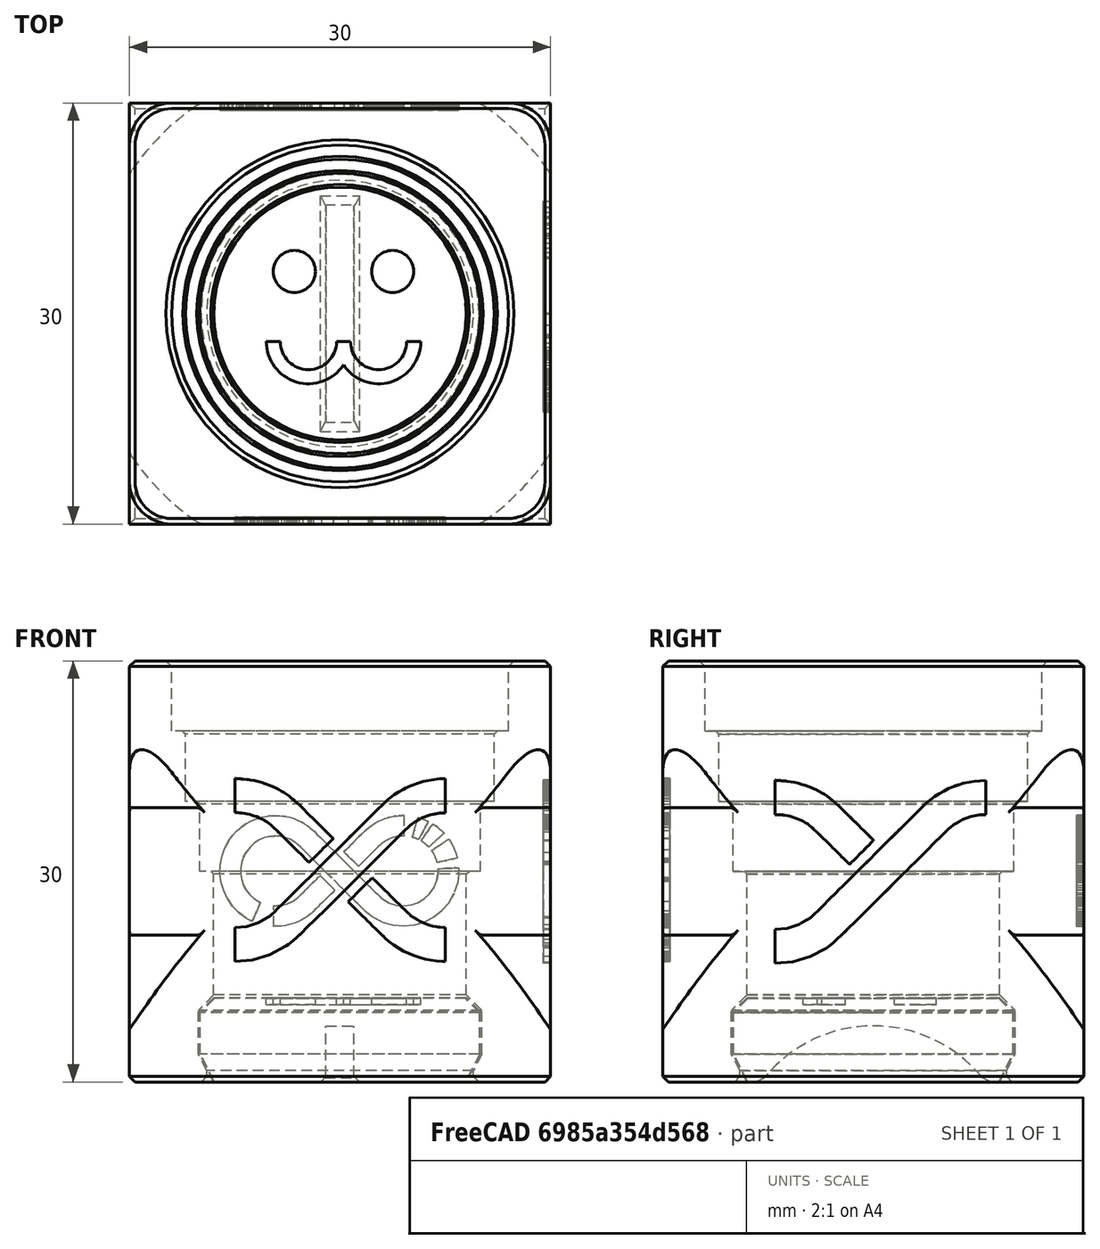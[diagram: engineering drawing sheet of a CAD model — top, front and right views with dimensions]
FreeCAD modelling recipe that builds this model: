
FCSTD DOCUMENT  (FreeCAD 0.19R24291 (Git))
Label: test-cube
License: Other
LicenseURL: GPL3
objects: Part::Cylinder×24, Part::Chamfer×20, Part::Cut×18, Part::MultiFuse×10, Part::Feature×8, TechDraw::DrawViewDimension×8, Part::Box×6, Part::MultiCommon×6, Part::Fillet×4, Part::FeaturePython×4, TechDraw::DrawViewPart×4, Part::Cone×2, TechDraw::DrawSVGTemplate×1, TechDraw::DrawViewSection×1, TechDraw::DrawViewBalloon×1, TechDraw::DrawPage×1
note: 102 computed .brp shape members not serialized (recipe doc carries the construction recipe); baked Part::Feature solids carry a one-line shape summary decoded from their .brp

FEATURE [Part::Box] Box  label="Cube"
  AttacherType = Attacher::AttachEngine3D
  Height = 12
  Length = 30
  Width = 30
FEATURE [Part::Cylinder] Cylinder
  Angle = 360
  AttacherType = Attacher::AttachEngine3D
  Height = 30
  Placement = pos=(15,15,0) rot=(0,0,1;0rad)
  Radius = 18
FEATURE [Part::Box] Box002  label="Cube002"
  AttacherType = Attacher::AttachEngine3D
  Height = 30
  Length = 30
  Width = 30
FEATURE [Part::Cone] Cone
  Angle = 360
  AttacherType = Attacher::AttachEngine3D
  Height = 23
  Placement = pos=(15,15,0) rot=(0,0,1;0rad)
  Radius1 = 23
  Radius2 = 12
FEATURE [Part::MultiCommon] Common001
  Shapes = -> [Cone,Box]
FEATURE [Part::Feature] Common001001
  Placement = pos=(30,0,30) rot=(0,1,0;3.14159rad)
  shape: bbox 36.87 x 36.87 x 12 mm, 10 faces (baked)
FEATURE [Part::MultiCommon] Common
  Shapes = -> [Box002,Cylinder]
FEATURE [Part::Fillet] Fillet
  Base = -> Common001001
  Edges = 4 edges r=3: [Edge11,Edge13,Edge15,Edge18]
FEATURE [Part::Cylinder] Cylinder001
  Angle = 360
  AttacherType = Attacher::AttachEngine3D
  Height = 12
  Placement = pos=(15,15,9) rot=(0,0,1;0rad)
  Radius = 20
FEATURE [Part::MultiCommon] Common001002
  Shapes = -> [Cylinder001,Common]
FEATURE [Part::Fillet] Fillet001
  Base = -> Common001002
  Edges = 8 edges r=1: [Edge9,Edge11,Edge13,Edge15,Edge17,Edge19,Edge21,Edge23]
FEATURE [Part::Chamfer] Chamfer
  Base = -> Common001
  Edges = 4 edges r=0.4: [Edge14,Edge17,Edge21,Edge24]
FEATURE [Part::Chamfer] Chamfer001
  Base = -> Fillet
  Edges = 8 edges r=0.4: [Edge6,Edge10,Edge20,Edge21,Edge22,Edge23,Edge24,Edge25]
FEATURE [Part::MultiFuse] Fusion
  Shapes = -> [Chamfer001,Chamfer,Fillet001]
FEATURE [Part::Cylinder] Cylinder004
  Angle = 360
  AttacherType = Attacher::AttachEngine3D
  Height = 7
  Placement = pos=(15,15,0) rot=(0,0,1;0rad)
  Radius = 10.1
FEATURE [Part::Cylinder] Cylinder005
  Angle = 360
  AttacherType = Attacher::AttachEngine3D
  Height = 6
  Placement = pos=(15,15,0) rot=(0,0,1;0rad)
  Radius = 10
FEATURE [Part::Chamfer] Chamfer002003
  Base = -> Cylinder005
  Edges = 1 edges: [Edge3 r1=2 r2=1]
FEATURE [Part::Chamfer] Chamfer002004
  Base = -> Chamfer002003
  Edges = 1 edges r=1: [Edge2]
FEATURE [Part::Chamfer] Chamfer002005
  Base = -> Cylinder004
  Edges = 1 edges: [Edge3 r1=2 r2=1]
FEATURE [Part::Cut] Cut
  Base = -> Fusion
  Tool = -> Chamfer002005
FEATURE [Part::Cylinder] Cylinder006
  Angle = 360
  AttacherType = Attacher::AttachEngine3D
  Height = 6
  Placement = pos=(15,15,0) rot=(0,0,1;0rad)
  Radius = 9.5
FEATURE [Part::Cut] Cut001
  Base = -> Cut
  Tool = -> Cylinder006
FEATURE [Part::Chamfer] Chamfer002006
  Base = -> Cut001
  Edges = 1 edges r=0.4: [Edge157]
FEATURE [Part::Chamfer] Chamfer002007
  Base = -> Chamfer002006
  Edges = 1 edges r=1.9: [Edge69]
FEATURE [Part::Cylinder] Cylinder007
  Angle = 360
  AttacherType = Attacher::AttachEngine3D
  Height = 2
  Placement = pos=(14,15,-6) rot=(0,1,0;1.5708rad)
  Radius = 10
FEATURE [Part::Cut] Cut002
  Base = -> Chamfer002004
  Tool = -> Cylinder007
FEATURE [Part::Chamfer] Chamfer002008
  Base = -> Cut002
  Edges = 4 edges r=0.4: [Edge8,Edge9,Edge10,Edge11]
FEATURE [Part::Cylinder] Cylinder008
  Angle = 360
  AttacherType = Attacher::AttachEngine3D
  Height = 33
  Placement = pos=(15,15,0) rot=(0,0,1;0rad)
  Radius = 9
FEATURE [Part::Cylinder] Cylinder009
  Angle = 360
  AttacherType = Attacher::AttachEngine3D
  Height = 33
  Placement = pos=(15,15,15) rot=(0,0,1;0rad)
  Radius = 10
FEATURE [Part::Cylinder] Cylinder010
  Angle = 360
  AttacherType = Attacher::AttachEngine3D
  Height = 33
  Placement = pos=(15,15,20) rot=(0,0,1;0rad)
  Radius = 11
FEATURE [Part::Cylinder] Cylinder011
  Angle = 360
  AttacherType = Attacher::AttachEngine3D
  Height = 33
  Placement = pos=(15,15,25) rot=(0,0,1;0rad)
  Radius = 12
FEATURE [Part::MultiFuse] Fusion001
  Shapes = -> [Cylinder011,Cylinder010,Cylinder009,Cylinder008]
FEATURE [Part::Cut] Cut003
  Base = -> Chamfer002007
  Refine = true
  Tool = -> Fusion001
FEATURE [Part::Chamfer] Chamfer002009
  Base = -> Cut003
  Edges = 3 edges r=0.2: [Edge81,Edge87,Edge102]
FEATURE [Part::Chamfer] Chamfer002010
  Base = -> Chamfer002009
  Edges = 1 edges r=0.4: [Edge79]
FEATURE [Part::Feature] Funky_Juttuli_Bombul_1_001001_solid  label="x"
  Placement = pos=(5.5,0.5,14.5) rot=(1,0,0;1.5708rad)
  shape: bbox 20 x 2 x 20 mm, 335 faces (baked)
FEATURE [Part::Feature] Funky_Juttuli_Bombul_2_001001_solid  label="y"
  Placement = pos=(29.5,-20,13.5) rot=(0.57735,0.57735,0.57735;2.0944rad)
  shape: bbox 2 x 20 x 20 mm, 246 faces (baked)
FEATURE [Part::Feature] Funky_Juttuli_Bombul001001_solid  label="logo"
  Placement = pos=(24.6,29.5,21) rot=(0,0.707107,0.707107;3.14159rad)
  shape: bbox 20 x 2 x 20 mm, 931 faces (baked)
FEATURE [Part::Cut] Cut004
  Base = -> Chamfer002010
  Tool = -> Funky_Juttuli_Bombul001001_solid
FEATURE [Part::Cut] Cut005
  Base = -> Cut004
  Tool = -> Funky_Juttuli_Bombul_2_001001_solid
FEATURE [Part::Cut] Cut006
  Base = -> Cut005
  Tool = -> Funky_Juttuli_Bombul_1_001001_solid
FEATURE [Part::FeaturePython] Tube  # WARN: FeaturePython — macro-defined, semantics opaque (R4)
  AttacherType = Attacher::AttachEngine3D
  Height = 1
  InnerRadius = 2
  OuterRadius = 3
  Placement = pos=(13,11.5,5.5) rot=(0,0,1;0rad)
FEATURE [Part::FeaturePython] Tube001  # WARN: FeaturePython — macro-defined, semantics opaque (R4)
  AttacherType = Attacher::AttachEngine3D
  Height = 1
  InnerRadius = 2
  OuterRadius = 3
  Placement = pos=(18,11.5,5.5) rot=(0,0,1;0rad)
FEATURE [Part::Cylinder] Cylinder012
  Angle = 360
  AttacherType = Attacher::AttachEngine3D
  Height = 1
  Placement = pos=(11.75,18,5.5) rot=(0,0,1;0rad)
  Radius = 1.5
FEATURE [Part::Cylinder] Cylinder013
  Angle = 360
  AttacherType = Attacher::AttachEngine3D
  Height = 1
  Placement = pos=(18.75,18,5.5) rot=(0,0,1;0rad)
  Radius = 1.5
FEATURE [Part::MultiFuse] Fusion002
  Shapes = -> [Tube001,Tube]
FEATURE [Part::Box] Box003  label="Cube003"
  AttacherType = Attacher::AttachEngine3D
  Height = 10
  Length = 16
  Placement = pos=(9.5,11.5,0) rot=(0,0,1;0rad)
  Width = 10
FEATURE [Part::Cut] Cut007
  Base = -> Fusion002
  Placement = pos=(-0.25,1.5,0) rot=(0,0,1;0rad)
  Tool = -> Box003
FEATURE [Part::MultiFuse] Fusion003
  Shapes = -> [Cut007,Cylinder013,Cylinder012]
FEATURE [Part::Cut] Cut008
  Base = -> Chamfer002008
  Refine = true
  Tool = -> Fusion003
FEATURE [TechDraw::DrawSVGTemplate] Template
  EditableTexts = Designed_by_Name=Chip; Drawing_number=-; FC-Date=2022-03-12; FC-SC=1:1.5; FC-SH=1/1; FC-Title=SnakeOil test cube; Subtitle=-; Weight=-
  Height = 210
  Orientation = 1
  Width = 297
FEATURE [Part::MultiFuse] Fusion004
  Shapes = -> [Cut008,Cut006]
FEATURE [TechDraw::DrawViewPart] View
  CoarseView = false
  Direction = (0.577,-0.577,0.577)
  Focus = 100
  HardHidden = false
  IsoCount = 0
  IsoHidden = false
  IsoVisible = false
  LockPosition = false
  Perspective = false
  Rotation = 0
  Scale = 1.5
  ScaleType = 0
  SeamHidden = false
  SeamVisible = true
  SmoothHidden = false
  SmoothVisible = true
  Source = -> [Fusion004]
  X = 53.1184
  XDirection = (0.707,0.707,0)
  Y = 155.57
FEATURE [TechDraw::DrawViewPart] View001
  CoarseView = false
  Direction = (0,0,1)
  Focus = 100
  HardHidden = false
  IsoCount = 0
  IsoHidden = false
  IsoVisible = false
  LockPosition = false
  Perspective = false
  Rotation = 0
  Scale = 1.5
  ScaleType = 0
  SeamHidden = false
  SeamVisible = true
  SmoothHidden = false
  SmoothVisible = true
  Source = -> [Fusion004]
  X = 142.764
  XDirection = (1,0,0)
  Y = 157.287
FEATURE [TechDraw::DrawViewPart] View002
  CoarseView = false
  Direction = (1,0,0)
  Focus = 100
  HardHidden = false
  IsoCount = 0
  IsoHidden = false
  IsoVisible = false
  LockPosition = false
  Perspective = false
  Rotation = 0
  Scale = 1.5
  ScaleType = 0
  SeamHidden = false
  SeamVisible = true
  SmoothHidden = false
  SmoothVisible = true
  Source = -> [Fusion004]
  X = 216.819
  XDirection = (0,1,0)
  Y = 157.983
FEATURE [TechDraw::DrawViewSection] SectionView  label="Section  - "
  BaseView = -> View002
  CoarseView = false
  CutSurfaceDisplay = 2
  Direction = (0,0,-1)
  FileGeomPattern = <path>
  FileHatchPattern = <path>
  Focus = 100
  FuseBeforeCut = false
  HardHidden = false
  HatchScale = 1
  IsoCount = 0
  IsoHidden = false
  IsoVisible = false
  LockPosition = false
  NameGeomPattern = Diamond
  Perspective = false
  Rotation = 0
  Scale = 1.5
  ScaleType = 0
  SeamHidden = false
  SeamVisible = true
  SectionDirection = 2
  SectionNormal = (0,0,-1)
  SectionOrigin = (15,15,15)
  SmoothHidden = false
  SmoothVisible = true
  Source = -> [Fusion004]
  X = 219.64
  XDirection = (0,1,0)
  Y = 91.1156
FEATURE [TechDraw::DrawViewDimension] Dimension
  Arbitrary = false
  ArbitraryTolerances = false
  EqualTolerance = true
  FormatSpec = %.2f
  FormatSpecOverTolerance = %+.2f
  FormatSpecUnderTolerance = %+.2f
  Inverted = false
  LockPosition = false
  MeasureType = 1
  OverTolerance = 0
  References2D = -> [View001]
  Rotation = 0
  ScaleType = 0
  TheoreticalExact = false
  Type = 1
  UnderTolerance = 0
  X = -0.329799
  Y = 34.2334
FEATURE [TechDraw::DrawViewDimension] Dimension001
  Arbitrary = false
  ArbitraryTolerances = false
  EqualTolerance = true
  FormatSpec = %.2f
  FormatSpecOverTolerance = %+.2f
  FormatSpecUnderTolerance = %+.2f
  Inverted = false
  LockPosition = false
  MeasureType = 1
  OverTolerance = 0
  References2D = -> [View001]
  Rotation = 0
  ScaleType = 0
  TheoreticalExact = false
  Type = 2
  UnderTolerance = 0
  X = 28.2238
  Y = 1.24591
FEATURE [TechDraw::DrawViewDimension] Dimension002
  Arbitrary = false
  ArbitraryTolerances = false
  EqualTolerance = true
  FormatSpec = ⌀%.2f
  FormatSpecOverTolerance = %+.2f
  FormatSpecUnderTolerance = %+.2f
  Inverted = false
  LockPosition = false
  MeasureType = 1
  OverTolerance = 0
  References2D = -> [View001]
  Rotation = 0
  ScaleType = 0
  TheoreticalExact = false
  Type = 5
  UnderTolerance = 0
  X = -30.9115
  Y = -26.0853
FEATURE [TechDraw::DrawViewDimension] Dimension003
  Arbitrary = false
  ArbitraryTolerances = false
  EqualTolerance = true
  FormatSpec = ⌀%.2f
  FormatSpecOverTolerance = %+.2f
  FormatSpecUnderTolerance = %+.2f
  Inverted = false
  LockPosition = false
  MeasureType = 1
  OverTolerance = 0
  References2D = -> [View001]
  Rotation = 0
  ScaleType = 0
  TheoreticalExact = false
  Type = 5
  UnderTolerance = 0
  X = -34.7096
  Y = -19.8838
FEATURE [TechDraw::DrawViewDimension] Dimension004
  Arbitrary = false
  ArbitraryTolerances = false
  EqualTolerance = true
  FormatSpec = ⌀%.2f
  FormatSpecOverTolerance = %+.2f
  FormatSpecUnderTolerance = %+.2f
  Inverted = false
  LockPosition = false
  MeasureType = 1
  OverTolerance = 0
  References2D = -> [View001]
  Rotation = 0
  ScaleType = 0
  TheoreticalExact = false
  Type = 5
  UnderTolerance = 0
  X = -38.0246
  Y = -13.1141
FEATURE [TechDraw::DrawViewDimension] Dimension005
  Arbitrary = false
  ArbitraryTolerances = false
  EqualTolerance = true
  FormatSpec = ⌀%.2f
  FormatSpecOverTolerance = %+.2f
  FormatSpecUnderTolerance = %+.2f
  Inverted = false
  LockPosition = false
  MeasureType = 1
  OverTolerance = 0
  References2D = -> [View001]
  Rotation = 0
  ScaleType = 0
  TheoreticalExact = false
  Type = 5
  UnderTolerance = 0
  X = -40.1538
  Y = -5.34316
FEATURE [TechDraw::DrawViewDimension] Dimension006
  Arbitrary = false
  ArbitraryTolerances = false
  EqualTolerance = true
  FormatSpec = %.2f
  FormatSpecOverTolerance = %+.2f
  FormatSpecUnderTolerance = %+.2f
  Inverted = false
  LockPosition = false
  MeasureType = 1
  OverTolerance = 0
  References2D = -> [View002]
  Rotation = 0
  ScaleType = 0
  TheoreticalExact = false
  Type = 2
  UnderTolerance = 0
  X = 36.8069
  Y = 0.263839
FEATURE [TechDraw::DrawViewDimension] Dimension007
  Arbitrary = false
  ArbitraryTolerances = false
  EqualTolerance = true
  FormatSpec = ⌀%.2f
  FormatSpecOverTolerance = %+.2f
  FormatSpecUnderTolerance = %+.2f
  Inverted = false
  LockPosition = false
  MeasureType = 1
  OverTolerance = 0
  References2D = -> [SectionView]
  Rotation = 0
  ScaleType = 0
  TheoreticalExact = false
  Type = 5
  UnderTolerance = 0
  X = 28.9918
  Y = -24.4224
FEATURE [TechDraw::DrawViewPart] View003
  CoarseView = false
  Direction = (0,0,-1)
  Focus = 100
  HardHidden = false
  IsoCount = 0
  IsoHidden = false
  IsoVisible = false
  LockPosition = false
  Perspective = false
  Rotation = 0
  Scale = 1.5
  ScaleType = 0
  SeamHidden = false
  SeamVisible = true
  SmoothHidden = false
  SmoothVisible = true
  Source = -> [Fusion004]
  X = 144.045
  XDirection = (1,0,0)
  Y = 90.5135
FEATURE [TechDraw::DrawViewBalloon] Balloon
  BubbleShape = 1
  EndType = 0
  EndTypeScale = 1
  KinkLength = 5
  LockPosition = false
  OriginX = -6.8407
  OriginY = 6.58082
  Rotation = 0
  ScaleType = 0
  ShapeScale = 1
  SourceView = -> View003
  Text = 0.15mm gap
  TextWrapLen = -1
  X = -25.924
  Y = 10.758
FEATURE [TechDraw::DrawPage] Page
  KeepUpdated = true
  NextBalloonIndex = 2
  ProjectionType = 0
  Template = -> Template
  Views = -> [View,View001,View002,SectionView,Dimension,Dimension001,Dimension002,Dimension003,Dimension004,Dimension005,Dimension006,Dimension007,View003,Balloon]
FEATURE [Part::Cylinder] Cylinder014
  Angle = 360
  AttacherType = Attacher::AttachEngine3D
  Height = 1
  Placement = pos=(18.75,18,5.5) rot=(0,0,1;0rad)
  Radius = 1.5
FEATURE [Part::Box] Box004  label="Cube004"
  AttacherType = Attacher::AttachEngine3D
  Height = 12
  Length = 30
  Width = 30
FEATURE [Part::Box] Box005  label="Cube005"
  AttacherType = Attacher::AttachEngine3D
  Height = 30
  Length = 30
  Width = 30
FEATURE [Part::Cylinder] Cylinder015
  Angle = 360
  AttacherType = Attacher::AttachEngine3D
  Height = 30
  Placement = pos=(15,15,0) rot=(0,0,1;0rad)
  Radius = 18
FEATURE [Part::Cone] Cone001
  Angle = 360
  AttacherType = Attacher::AttachEngine3D
  Height = 23
  Placement = pos=(15,15,0) rot=(0,0,1;0rad)
  Radius1 = 23
  Radius2 = 12
FEATURE [Part::Cylinder] Cylinder016
  Angle = 360
  AttacherType = Attacher::AttachEngine3D
  Height = 12
  Placement = pos=(15,15,9) rot=(0,0,1;0rad)
  Radius = 20
FEATURE [Part::MultiCommon] Common001003
  Shapes = -> [Cone001,Box004]
FEATURE [Part::Feature] Common001004
  Placement = pos=(30,0,30) rot=(0,1,0;3.14159rad)
  shape: bbox 36.87 x 36.87 x 12 mm, 10 faces (baked)
FEATURE [Part::MultiCommon] Common001005
  Shapes = -> [Box005,Cylinder015]
FEATURE [Part::Fillet] Fillet002
  Base = -> Common001004
  Edges = 4 edges r=3: [Edge11,Edge13,Edge15,Edge18]
FEATURE [Part::MultiCommon] Common001006
  Shapes = -> [Cylinder016,Common001005]
FEATURE [Part::Fillet] Fillet003
  Base = -> Common001006
  Edges = 8 edges r=1: [Edge9,Edge11,Edge13,Edge15,Edge17,Edge19,Edge21,Edge23]
FEATURE [Part::Cylinder] Cylinder017
  Angle = 360
  AttacherType = Attacher::AttachEngine3D
  Height = 33
  Placement = pos=(15,15,15) rot=(0,0,1;0rad)
  Radius = 10
FEATURE [Part::Cylinder] Cylinder018
  Angle = 360
  AttacherType = Attacher::AttachEngine3D
  Height = 6
  Placement = pos=(15,15,0) rot=(0,0,1;0rad)
  Radius = 9.5
FEATURE [Part::Cylinder] Cylinder019
  Angle = 360
  AttacherType = Attacher::AttachEngine3D
  Height = 33
  Placement = pos=(15,15,0) rot=(0,0,1;0rad)
  Radius = 9
FEATURE [Part::Feature] Funky_Juttuli_Bombul_1_001001_solid001  label="x001"
  Placement = pos=(5.5,0.5,14.5) rot=(1,0,0;1.5708rad)
  shape: bbox 20 x 2 x 20 mm, 335 faces (baked)
FEATURE [Part::Cylinder] Cylinder020
  Angle = 360
  AttacherType = Attacher::AttachEngine3D
  Height = 33
  Placement = pos=(15,15,20) rot=(0,0,1;0rad)
  Radius = 11
FEATURE [Part::FeaturePython] Tube002  # WARN: FeaturePython — macro-defined, semantics opaque (R4)
  AttacherType = Attacher::AttachEngine3D
  Height = 1
  InnerRadius = 2
  OuterRadius = 3
  Placement = pos=(18,11.5,5.5) rot=(0,0,1;0rad)
FEATURE [Part::Feature] Funky_Juttuli_Bombul001001_solid001  label="logo001"
  Placement = pos=(24.6,29.5,21) rot=(0,0.707107,0.707107;3.14159rad)
  shape: bbox 20 x 2 x 20 mm, 931 faces (baked)
FEATURE [Part::Cylinder] Cylinder021
  Angle = 360
  AttacherType = Attacher::AttachEngine3D
  Height = 5.95
  Placement = pos=(15,15,0) rot=(0,0,1;0rad)
  Radius = 9.95
FEATURE [Part::Cylinder] Cylinder022
  Angle = 360
  AttacherType = Attacher::AttachEngine3D
  Height = 7
  Placement = pos=(15,15,0) rot=(0,0,1;0rad)
  Radius = 10.1
FEATURE [Part::Chamfer] Chamfer002014
  Base = -> Cylinder022
  Edges = 1 edges: [Edge3 r1=2 r2=1]
FEATURE [Part::Cylinder] Cylinder023
  Angle = 360
  AttacherType = Attacher::AttachEngine3D
  Height = 33
  Placement = pos=(15,15,25) rot=(0,0,1;0rad)
  Radius = 12
FEATURE [Part::Cylinder] Cylinder024
  Angle = 360
  AttacherType = Attacher::AttachEngine3D
  Height = 2
  Placement = pos=(14,15,-6) rot=(0,1,0;1.5708rad)
  Radius = 10
FEATURE [Part::Chamfer] Chamfer002019
  Base = -> Fillet002
  Edges = 8 edges r=0.4: [Edge6,Edge10,Edge20,Edge21,Edge22,Edge23,Edge24,Edge25]
FEATURE [Part::MultiFuse] Fusion007
  Shapes = -> [Cylinder023,Cylinder020,Cylinder017,Cylinder019]
FEATURE [Part::Chamfer] Chamfer002020
  Base = -> Common001003
  Edges = 4 edges r=0.4: [Edge14,Edge17,Edge21,Edge24]
FEATURE [Part::MultiFuse] Fusion005
  Shapes = -> [Chamfer002019,Chamfer002020,Fillet003]
FEATURE [Part::Cut] Cut014
  Base = -> Fusion005
  Tool = -> Chamfer002014
FEATURE [Part::Cut] Cut009
  Base = -> Cut014
  Tool = -> Cylinder018
FEATURE [Part::Chamfer] Chamfer002015
  Base = -> Cut009
  Edges = 1 edges r=0.4: [Edge157]
FEATURE [Part::Chamfer] Chamfer002017
  Base = -> Chamfer002015
  Edges = 1 edges r=1.9: [Edge69]
FEATURE [Part::Cut] Cut010
  Base = -> Chamfer002017
  Refine = true
  Tool = -> Fusion007
FEATURE [Part::Chamfer] Chamfer002016
  Base = -> Cut010
  Edges = 3 edges r=0.2: [Edge81,Edge87,Edge102]
FEATURE [Part::Chamfer] Chamfer002011
  Base = -> Chamfer002016
  Edges = 1 edges r=0.4: [Edge79]
FEATURE [Part::Cut] Cut013
  Base = -> Chamfer002011
  Tool = -> Funky_Juttuli_Bombul001001_solid001
FEATURE [Part::Feature] Funky_Juttuli_Bombul_2_001001_solid001  label="y001"
  Placement = pos=(29.5,-20,13.5) rot=(0.57735,0.57735,0.57735;2.0944rad)
  shape: bbox 2 x 20 x 20 mm, 246 faces (baked)
FEATURE [Part::Cut] Cut011
  Base = -> Cut013
  Tool = -> Funky_Juttuli_Bombul_2_001001_solid001
FEATURE [Part::Cut] Cut015
  Base = -> Cut011
  Tool = -> Funky_Juttuli_Bombul_1_001001_solid001
FEATURE [Part::Box] Box006  label="Cube006"
  AttacherType = Attacher::AttachEngine3D
  Height = 10
  Length = 16
  Placement = pos=(9.5,11.5,0) rot=(0,0,1;0rad)
  Width = 10
FEATURE [Part::FeaturePython] Tube003  # WARN: FeaturePython — macro-defined, semantics opaque (R4)
  AttacherType = Attacher::AttachEngine3D
  Height = 1
  InnerRadius = 2
  OuterRadius = 3
  Placement = pos=(13,11.5,5.5) rot=(0,0,1;0rad)
FEATURE [Part::MultiFuse] Fusion006
  Shapes = -> [Tube002,Tube003]
FEATURE [Part::Cylinder] Cylinder025
  Angle = 360
  AttacherType = Attacher::AttachEngine3D
  Height = 1
  Placement = pos=(11.75,18,5.5) rot=(0,0,1;0rad)
  Radius = 1.5
FEATURE [Part::Cut] Cut016
  Base = -> Fusion006
  Placement = pos=(-0.25,1.5,0) rot=(0,0,1;0rad)
  Tool = -> Box006
FEATURE [Part::MultiFuse] Fusion008
  Shapes = -> [Cut016,Cylinder014,Cylinder025]
FEATURE [Part::Chamfer] Chamfer002021
  Base = -> Cylinder021
  Edges = 1 edges: [Edge3 r1=2 r2=1]
FEATURE [Part::Chamfer] Chamfer002022
  Base = -> Chamfer002021
  Edges = 1 edges r=1: [Edge2]
FEATURE [Part::Cut] Cut017
  Base = -> Chamfer002022
  Tool = -> Cylinder024
FEATURE [Part::Cut] Cut018
  Base = -> Cut017
  Tool = -> Fusion008
FEATURE [Part::Chamfer] Chamfer002023
  Base = -> Cut018
  Edges = 4 edges r=0.4: [Edge17,Edge18,Edge19,Edge20]
FEATURE [Part::MultiFuse] Fusion009
  Shapes = -> [Cut015,Chamfer002023]
note: 2 file-system paths scrubbed to <path> (originals preserved in the JSON sidecar)
